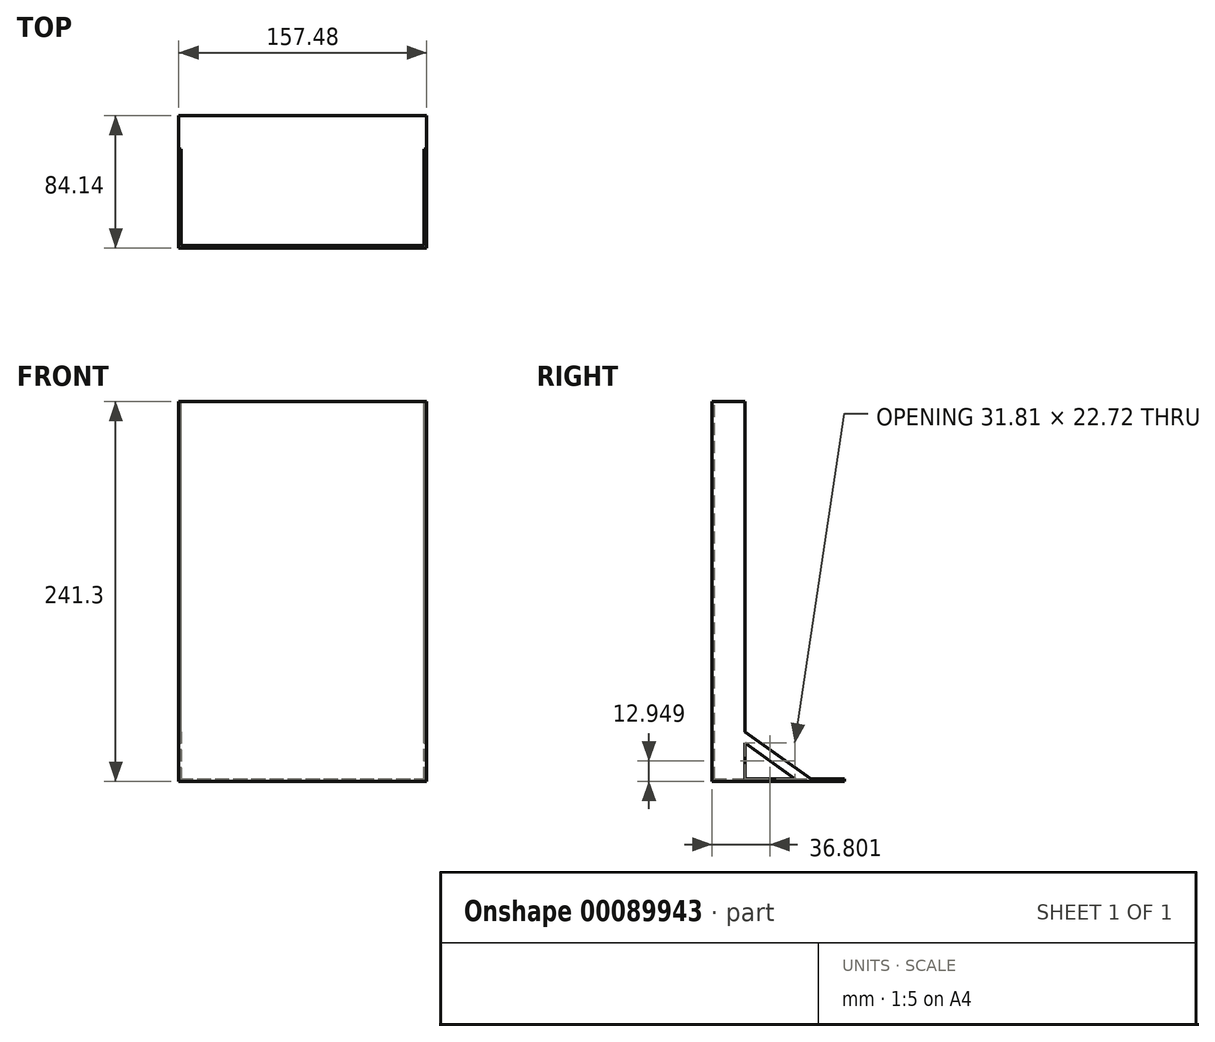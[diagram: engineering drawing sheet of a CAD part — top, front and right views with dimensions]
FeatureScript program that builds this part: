
annotation { "Feature Type Name" : "Feature", "Feature Type Description" : "" }
export const myFeature = defineFeature(function(context is Context, id is Id, definition is map)
    precondition{}
    {
        {
            var Q0;
            Q0=qCreatedBy(makeId("Top.planeOp"),FACE);
            var sketch = newSketch(context, id + "F0", { "sketchPlane" : qUnion([Q0])});
            skLineSegment(sketch, "E0.bottom", {"start": v(0, 0) * mm, "end": v(157.48, 0) * mm});
            skLineSegment(sketch, "E0.top", {"start": v(0, 82.55) * mm, "end": v(157.48, 82.55) * mm});
            skLineSegment(sketch, "E0.left", {"start": v(0, 0) * mm, "end": v(0, 82.55) * mm});
            skLineSegment(sketch, "E0.right", {"start": v(157.48, 0) * mm, "end": v(157.48, 82.55) * mm});
            skSolve(sketch);
        }
        {
            var Q0;
            Q0 = qSketchRegion(id + "F0", true);
            var Q1;
            Q1=makeQuery(id+"F0.imprint","IMPRINT",FACE,{"disambiguationData":[TD([[makeQuery(id+"F0.imprint","IMPRINT",EDGE,{"derivedFrom":sQuery(id+"F0.wireOp",EDGE,"E0.bottom")}),1.0]])]});
            extrude(context, id + "F1", {"entities" : qUnion([Q0, Q1]), "depth" : 1.59 * mm});
        }
        {
            var Q0;
            Q0=qCreatedBy(makeId("Front.planeOp"),FACE);
            var sketch = newSketch(context, id + "F2", { "sketchPlane" : qUnion([Q0])});
            skLineSegment(sketch, "E1.bottom", {"start": v(0, 0) * mm, "end": v(157.48, 0) * mm});
            skLineSegment(sketch, "E1.top", {"start": v(0, 241.3) * mm, "end": v(157.48, 241.3) * mm});
            skLineSegment(sketch, "E1.left", {"start": v(0, 0) * mm, "end": v(0, 241.3) * mm});
            skLineSegment(sketch, "E1.right", {"start": v(157.48, 0) * mm, "end": v(157.48, 241.3) * mm});
            skSolve(sketch);
        }
        {
            var Q0;
            Q0=makeQuery(id+"F2.imprint","IMPRINT",FACE,{"disambiguationData":[TD([[makeQuery(id+"F2.imprint","IMPRINT",EDGE,{"derivedFrom":sQuery(id+"F2.wireOp",EDGE,"E1.bottom")}),1.0]])]});
            extrude(context, id + "F3", {"entities" : qUnion([Q0]), "operationType" : NewBodyOperationType.ADD, "depth" : 1.59 * mm});
        }
        {
            var Q0;
            Q0=qCreatedBy(makeId("Right.planeOp"),FACE);
            var sketch = newSketch(context, id + "F4", { "sketchPlane" : qUnion([Q0])});
            skLineSegment(sketch, "E2.bottom", {"start": v(0, 0) * mm, "end": v(19.3, 0) * mm});
            skLineSegment(sketch, "E2.top", {"start": v(0, 241.3) * mm, "end": v(19.3, 241.3) * mm});
            skLineSegment(sketch, "E2.left", {"start": v(0, 0) * mm, "end": v(0, 241.3) * mm});
            skLineSegment(sketch, "E2.right", {"start": v(19.3, 0) * mm, "end": v(19.3, 241.3) * mm});
            skSolve(sketch);
        }
        {
            var Q0;
            Q0 = qSketchRegion(id + "F4", true);
            extrude(context, id + "F5", {"entities" : qUnion([Q0]), "operationType" : NewBodyOperationType.ADD, "depth" : 1.59 * mm});
        }
        {
            var Q0;
            Q0=makeQuery(id+"F1.opExtrude","CAP_VERTEX",VERTEX,{"disambiguationData":[OSD([sQuery(id+"F0.wireOp",EDGE,"E0.top"),sQuery(id+"F0.wireOp",EDGE,"E0.right")])],"isStart":false});
            var Q1;
            Q1=makeQuery(id+"F1.opExtrude","CAP_VERTEX",VERTEX,{"disambiguationData":[OSD([sQuery(id+"F0.wireOp",EDGE,"E0.bottom"),sQuery(id+"F0.wireOp",EDGE,"E0.right")])],"isStart":false});
            var Q2;
            Q2=makeQuery(id+"F3.opExtrude","CAP_VERTEX",VERTEX,{"disambiguationData":[OSD([sQuery(id+"F2.wireOp",EDGE,"E1.top"),sQuery(id+"F2.wireOp",EDGE,"E1.right")])],"isStart":true});
            cPlane(context, id + "F6", {"entities" : qUnion([Q0, Q1, Q2]), "cplaneType" : CPlaneType.THREE_POINT, "offset" : 152.4 * mm, "width" : 152.4 * mm, "height" : 152.4 * mm});
        }
        {
            var Q0;
            Q0=qCreatedBy(id+"F6.planeOp",FACE);
            var sketch = newSketch(context, id + "F7", { "sketchPlane" : qUnion([Q0])});
            skLineSegment(sketch, "E3.bottom", {"start": v(0, 1.78) * mm, "end": v(24.97, 1.78) * mm});
            skLineSegment(sketch, "E3.top", {"start": v(0, 240.95) * mm, "end": v(24.97, 240.95) * mm});
            skLineSegment(sketch, "E3.left", {"start": v(0, 1.78) * mm, "end": v(0, 240.95) * mm});
            skLineSegment(sketch, "E3.right", {"start": v(24.97, 1.78) * mm, "end": v(24.97, 240.95) * mm});
            skSolve(sketch);
        }
        {
            var Q0;
            Q0 = qSketchRegion(id + "F7", true);
            extrude(context, id + "F8", {"entities" : qUnion([Q0]), "oppositeDirection" : true, "depth" : 1.59 * mm});
        }
        {
            var Q0;
            Q0=makeQuery(id+"F8.opExtrude","SWEPT_BODY",BODY,{"disambiguationData":[OSD([sQuery(id+"F7.wireOp",EDGE,"E3.bottom"),sQuery(id+"F7.wireOp",EDGE,"E3.top"),sQuery(id+"F7.wireOp",EDGE,"E3.left"),sQuery(id+"F7.wireOp",EDGE,"E3.right")])]});
            deleteBodies(context, id + "F9", {"entities" : qUnion([Q0])});
        }
        {
            var Q0;
            Q0=qCreatedBy(id+"F6.planeOp",FACE);
            var sketch = newSketch(context, id + "F10", { "sketchPlane" : qUnion([Q0])});
            skLineSegment(sketch, "E4.bottom", {"start": v(0, 0) * mm, "end": v(19.3, 0) * mm});
            skLineSegment(sketch, "E4.top", {"start": v(0, 241.3) * mm, "end": v(19.3, 241.3) * mm});
            skLineSegment(sketch, "E4.left", {"start": v(0, 0) * mm, "end": v(0, 241.3) * mm});
            skLineSegment(sketch, "E4.right", {"start": v(19.3, 0) * mm, "end": v(19.3, 241.3) * mm});
            skSolve(sketch);
        }
        {
            var Q0;
            Q0=makeQuery(id+"F10.imprint","IMPRINT",FACE,{"disambiguationData":[TD([[makeQuery(id+"F10.imprint","IMPRINT",EDGE,{"derivedFrom":sQuery(id+"F10.wireOp",EDGE,"E4.bottom")}),1.0]])]});
            extrude(context, id + "F11", {"entities" : qUnion([Q0]), "operationType" : NewBodyOperationType.ADD, "oppositeDirection" : true, "depth" : 1.59 * mm});
        }
        {
            var Q0;
            Q0=qCreatedBy(id+"F6.planeOp",FACE);
            var sketch = newSketch(context, id + "F12", { "sketchPlane" : qUnion([Q0])});
            skLineSegment(sketch, "E5", {"start": v(0, 45.36) * mm, "end": v(63.5, 0) * mm});
            skLineSegment(sketch, "E6", {"start": v(63.5, 0) * mm, "end": v(53.34, 0) * mm});
            skLineSegment(sketch, "E7", {"start": v(53.34, 0) * mm, "end": v(0, 38.1) * mm});
            skLineSegment(sketch, "E8", {"start": v(0, 38.1) * mm, "end": v(0, 45.36) * mm});
            skSolve(sketch);
        }
        {
            var Q0;
            Q0=makeQuery(id+"F12.imprint","IMPRINT",FACE,{"disambiguationData":[TD([[makeQuery(id+"F12.imprint","IMPRINT",EDGE,{"derivedFrom":sQuery(id+"F12.wireOp",EDGE,"E5")}),-1.0]])]});
            extrude(context, id + "F13", {"entities" : qUnion([Q0]), "operationType" : NewBodyOperationType.ADD, "oppositeDirection" : true, "depth" : 1.59 * mm});
        }
        {
            var Q0;
            Q0=qCreatedBy(makeId("Right.planeOp"),FACE);
            var sketch = newSketch(context, id + "F14", { "sketchPlane" : qUnion([Q0])});
            skLineSegment(sketch, "E9", {"start": v(0, 45.36) * mm, "end": v(63.5, 0) * mm});
            skLineSegment(sketch, "E10", {"start": v(63.5, 0) * mm, "end": v(53.34, 0) * mm});
            skLineSegment(sketch, "E11", {"start": v(53.34, 0) * mm, "end": v(0, 38.1) * mm});
            skLineSegment(sketch, "E12", {"start": v(0, 38.1) * mm, "end": v(0, 45.36) * mm});
            skSolve(sketch);
        }
        {
            var Q0;
            Q0 = qSketchRegion(id + "F14", true);
            extrude(context, id + "F15", {"entities" : qUnion([Q0]), "operationType" : NewBodyOperationType.ADD, "depth" : 1.59 * mm});
        }
    });
